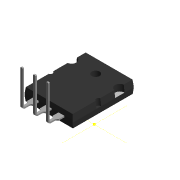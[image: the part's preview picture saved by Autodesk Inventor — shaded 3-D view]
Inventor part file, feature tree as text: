
AUTODESK INVENTOR PART (.ipt)
format: ipt  version: 2016 SP2 (Build 200236200, 236)  size: 329,728 bytes
history: native  units: mm
features: sketch x3, other x2, extrude x1
ambient origin geometry x8: Origin, YZ Plane, XZ Plane, XY Plane, X Axis, Y Axis, Z Axis, Center Point
bodies: Solid1 (feature_tree)
feature tree (6):
  sketch  "Sketch1"  dims[d0=0.2mm d1=0.0mm d3=5.0mm]
  extrude  "Extrusion1"  Depth=5.0mm
  other  "Bend Part1"
  sketch  "Sketch2"  dims[d4=0.5mm d5=15.70796mm]
  sketch  "Sketch4"
  other  "Wytnij-wyciagniecie2"
